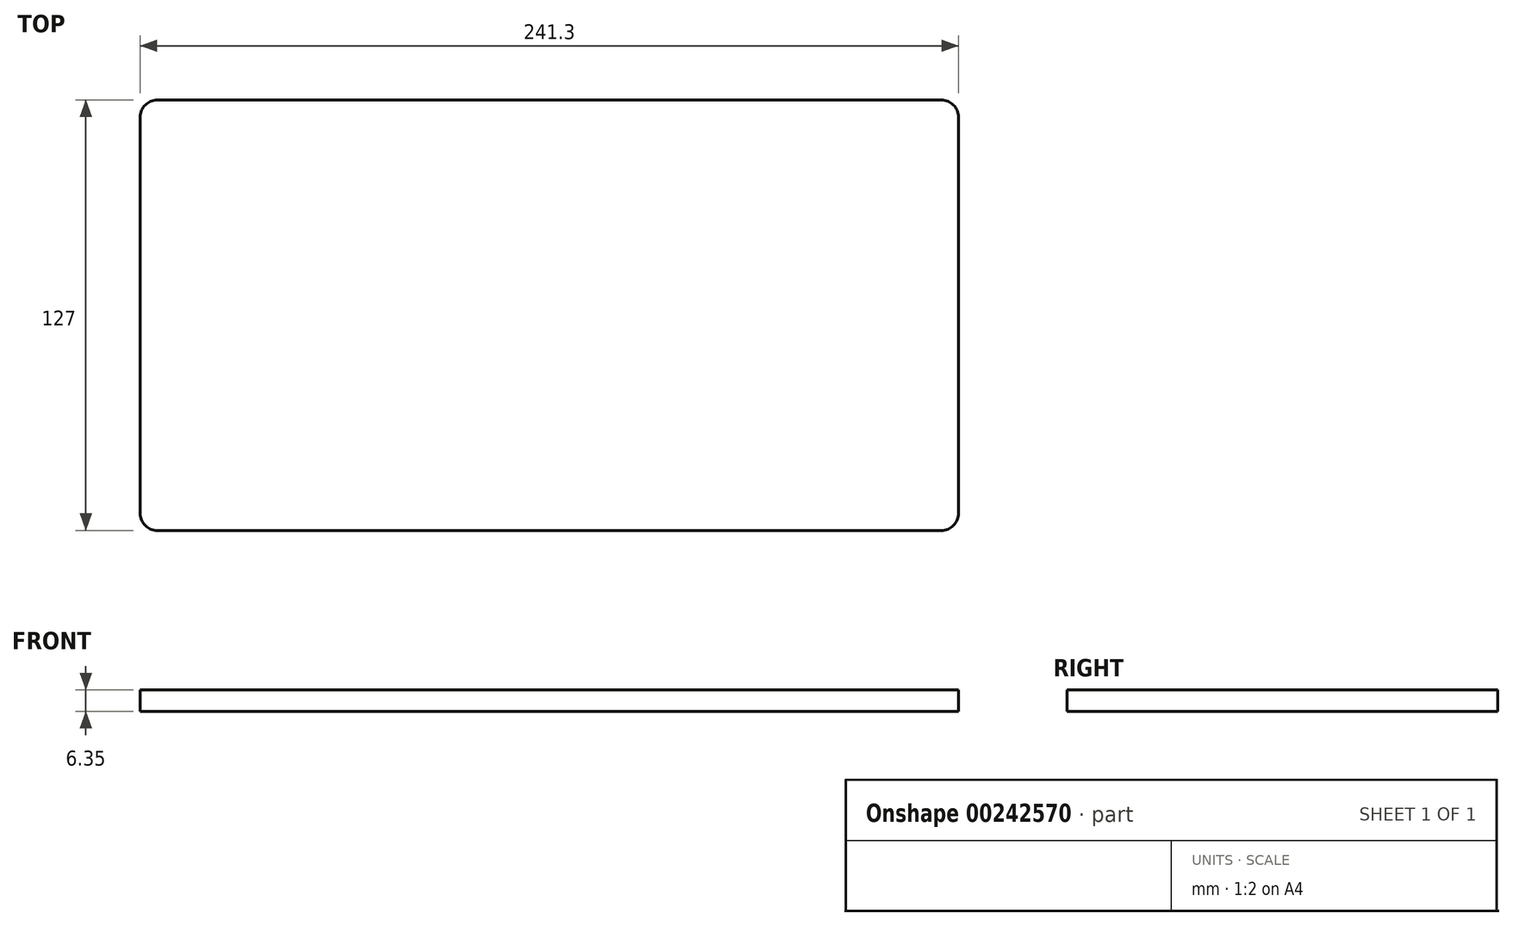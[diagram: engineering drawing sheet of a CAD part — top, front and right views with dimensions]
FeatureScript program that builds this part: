
annotation { "Feature Type Name" : "Feature", "Feature Type Description" : "" }
export const myFeature = defineFeature(function(context is Context, id is Id, definition is map)
    precondition{}
    {
        {
            var Q0;
            Q0=qCreatedBy(makeId("Top.planeOp"),FACE);
            var sketch = newSketch(context, id + "F0", { "sketchPlane" : qUnion([Q0])});
            skLineSegment(sketch, "E0.bottom", {"start": v(222.25, 222.25) * mm, "end": v(-222.25, 222.25) * mm, "construction": true});
            skLineSegment(sketch, "E0.top", {"start": v(222.25, -222.25) * mm, "end": v(-222.25, -222.25) * mm, "construction": true});
            skLineSegment(sketch, "E0.left", {"start": v(222.25, 222.25) * mm, "end": v(222.25, -222.25) * mm, "construction": true});
            skLineSegment(sketch, "E0.right", {"start": v(-222.25, 222.25) * mm, "end": v(-222.25, -222.25) * mm, "construction": true});
            skPoint(sketch, "E0.middle", {"position": v(0, 0) * mm});
            skLineSegment(sketch, "E1.bottom", {"start": v(-222.25, 222.25) * mm, "end": v(-120.65, 222.25) * mm});
            skLineSegment(sketch, "E1.top", {"start": v(-222.25, -222.25) * mm, "end": v(-120.65, -222.25) * mm});
            skLineSegment(sketch, "E1.left", {"start": v(-222.25, 222.25) * mm, "end": v(-222.25, -222.25) * mm});
            skLineSegment(sketch, "E1.right", {"start": v(-120.65, 222.25) * mm, "end": v(-120.65, -222.25) * mm});
            skLineSegment(sketch, "E2.bottom", {"start": v(222.25, 222.25) * mm, "end": v(120.65, 222.25) * mm});
            skLineSegment(sketch, "E2.top", {"start": v(222.25, -222.25) * mm, "end": v(120.65, -222.25) * mm});
            skLineSegment(sketch, "E2.left", {"start": v(222.25, 222.25) * mm, "end": v(222.25, -222.25) * mm});
            skLineSegment(sketch, "E2.right", {"start": v(120.65, 222.25) * mm, "end": v(120.65, -222.25) * mm});
            skLineSegment(sketch, "E3.bottom", {"start": v(-120.65, 95.25) * mm, "end": v(120.65, 95.25) * mm});
            skLineSegment(sketch, "E3.top", {"start": v(-120.65, -31.75) * mm, "end": v(120.65, -31.75) * mm});
            skLineSegment(sketch, "E3.left", {"start": v(-120.65, 95.25) * mm, "end": v(-120.65, -31.75) * mm});
            skLineSegment(sketch, "E3.right", {"start": v(120.65, 95.25) * mm, "end": v(120.65, -31.75) * mm});
            skLineSegment(sketch, "E4", {"start": v(-120.65, 222.25) * mm, "end": v(-222.25, 120.65) * mm});
            skLineSegment(sketch, "E5", {"start": v(120.65, 222.25) * mm, "end": v(222.25, 120.65) * mm});
            skLineSegment(sketch, "E6", {"start": v(120.65, -222.25) * mm, "end": v(222.25, -120.65) * mm});
            skLineSegment(sketch, "E7", {"start": v(-120.65, -222.25) * mm, "end": v(-222.25, -120.65) * mm});
            skPoint(sketch, "E8", {"position": v(-171.45, 171.45) * mm});
            skPoint(sketch, "E9", {"position": v(171.45, 171.45) * mm});
            skPoint(sketch, "E10", {"position": v(171.45, -171.45) * mm});
            skPoint(sketch, "E11", {"position": v(-171.45, -171.45) * mm});
            skLineSegment(sketch, "E12", {"start": v(-171.45, 171.45) * mm, "end": v(-161.57, 161.57) * mm});
            skLineSegment(sketch, "E13", {"start": v(-184.2, 138.94) * mm, "end": v(-138.94, 184.2) * mm});
            skLineSegment(sketch, "E14", {"start": v(-171.45, 171.45) * mm, "end": v(-198.15, 198.15) * mm});
            skLineSegment(sketch, "E15", {"start": v(-223.6, 172.7) * mm, "end": v(-172.7, 223.6) * mm});
            skCircle(sketch, "E16", {"center": v(-138.94, 184.2) * mm, "radius": 1.85 * mm});
            skCircle(sketch, "E17", {"center": v(-184.2, 138.94) * mm, "radius": 1.85 * mm});
            skCircle(sketch, "E18.MirrorC", {"center": v(138.94, 184.2) * mm, "radius": 1.85 * mm});
            skCircle(sketch, "E19.MirrorC", {"center": v(184.2, 138.94) * mm, "radius": 1.85 * mm});
            skCircle(sketch, "E20.MirrorC", {"center": v(-184.2, -138.94) * mm, "radius": 1.85 * mm});
            skCircle(sketch, "E21.MirrorC", {"center": v(-138.94, -184.2) * mm, "radius": 1.85 * mm});
            skCircle(sketch, "E22.MirrorC", {"center": v(138.94, -184.2) * mm, "radius": 1.85 * mm});
            skCircle(sketch, "E23.MirrorC", {"center": v(184.2, -138.94) * mm, "radius": 1.85 * mm});
            skSolve(sketch);
        }
        {
            var Q0;
            Q0=makeQuery(id+"F0.imprint","IMPRINT",FACE,{"disambiguationData":[TD([[makeQuery(id+"F0.imprint","IMPRINT",EDGE,{"derivedFrom":sQuery(id+"F0.wireOp",EDGE,"E3.bottom")}),-1.0]])]});
            var Q1;
            {var subQ0=sQuery(id+"F0.wireOp",EDGE,"E3.left");Q1=makeQuery(id+"F0.imprint","IMPRINT",FACE,{"disambiguationData":[TD([[makeQuery(id+"F0.imprint","IMPRINT",EDGE,{"derivedFrom":subQ0}),-1.0]])]});}
            var Q2;
            {var subQ2=sQuery(id+"F0.wireOp",EDGE,"E3.right");Q2=makeQuery(id+"F0.imprint","IMPRINT",FACE,{"disambiguationData":[TD([[makeQuery(id+"F0.imprint","IMPRINT",EDGE,{"derivedFrom":subQ2}),1.0]])]});}
            extrude(context, id + "F1", {"entities" : qUnion([Q0, Q1, Q2]), "depth" : 6.35 * mm});
        }
        {
            var Q0;
            Q0=makeQuery(id+"F1.opExtrude","SWEPT_EDGE",EDGE,{"disambiguationData":[OSD([sQuery(id+"F0.wireOp",EDGE,"E1.top"),sQuery(id+"F0.wireOp",EDGE,"E1.right"),sQuery(id+"F0.wireOp",EDGE,"E7")])]});
            var Q1;
            Q1=makeQuery(id+"F1.opExtrude","SWEPT_EDGE",EDGE,{"disambiguationData":[OSD([sQuery(id+"F0.wireOp",EDGE,"E2.top"),sQuery(id+"F0.wireOp",EDGE,"E2.right"),sQuery(id+"F0.wireOp",EDGE,"E6")])]});
            var Q2;
            Q2=makeQuery(id+"F1.opExtrude","SWEPT_EDGE",EDGE,{"disambiguationData":[OSD([sQuery(id+"F0.wireOp",EDGE,"E2.bottom"),sQuery(id+"F0.wireOp",EDGE,"E2.right"),sQuery(id+"F0.wireOp",EDGE,"E5")])]});
            var Q3;
            Q3=makeQuery(id+"F1.opExtrude","SWEPT_EDGE",EDGE,{"disambiguationData":[OSD([sQuery(id+"F0.wireOp",EDGE,"E1.bottom"),sQuery(id+"F0.wireOp",EDGE,"E1.right"),sQuery(id+"F0.wireOp",EDGE,"E4")])]});
            var Q4;
            Q4=makeQuery(id+"F1.opExtrude","SWEPT_EDGE",EDGE,{"disambiguationData":[OSD([sQuery(id+"F0.wireOp",EDGE,"E2.left"),sQuery(id+"F0.wireOp",EDGE,"E5")])]});
            var Q5;
            Q5=makeQuery(id+"F1.opExtrude","SWEPT_EDGE",EDGE,{"disambiguationData":[OSD([sQuery(id+"F0.wireOp",EDGE,"E2.left"),sQuery(id+"F0.wireOp",EDGE,"E6")])]});
            var Q6;
            Q6=makeQuery(id+"F1.opExtrude","SWEPT_EDGE",EDGE,{"disambiguationData":[OSD([sQuery(id+"F0.wireOp",EDGE,"E1.left"),sQuery(id+"F0.wireOp",EDGE,"E4")])]});
            var Q7;
            Q7=makeQuery(id+"F1.opExtrude","SWEPT_EDGE",EDGE,{"disambiguationData":[OSD([sQuery(id+"F0.wireOp",EDGE,"E1.left"),sQuery(id+"F0.wireOp",EDGE,"E7")])]});
            fillet(context, id + "F2", {"entities" : qUnion([Q0, Q1, Q2, Q3, Q4, Q5, Q6, Q7]), "radius" : 5.08 * mm, "tangentPropagation" : true, "allowEdgeOverflow" : false});
        }
    });
